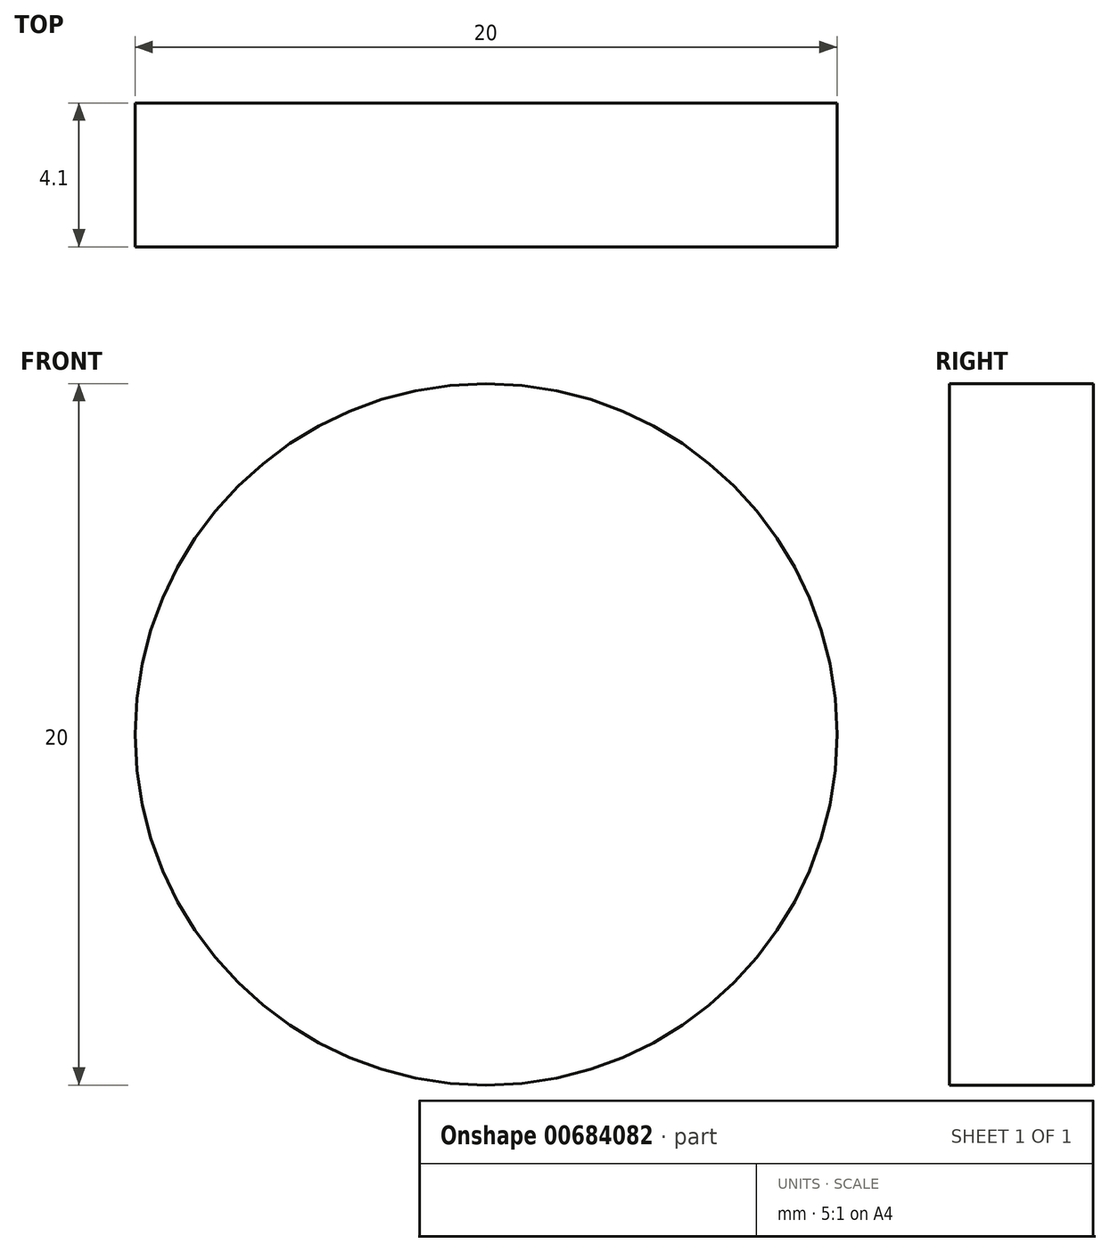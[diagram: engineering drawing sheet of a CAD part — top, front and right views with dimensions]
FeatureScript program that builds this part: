
annotation { "Feature Type Name" : "Feature", "Feature Type Description" : "" }
export const myFeature = defineFeature(function(context is Context, id is Id, definition is map)
    precondition{}
    {
        {
            var Q0;
            Q0=qCreatedBy(makeId("Front.planeOp"),FACE);
            var sketch = newSketch(context, id + "F0", { "sketchPlane" : qUnion([Q0])});
            skCircle(sketch, "E0", {"center": v(0, 0) * mm, "radius": 10 * mm});
            skSolve(sketch);
        }
        {
            var Q0;
            Q0=makeQuery(id+"F0.imprint","IMPRINT",FACE,{"disambiguationData":[TD([[makeQuery(id+"F0.imprint","IMPRINT",EDGE,{"derivedFrom":sQuery(id+"F0.wireOp",EDGE,"E0")}),1.0]])]});
            extrude(context, id + "F1", {"entities" : qUnion([Q0]), "depth" : 4.1 * mm, "offsetDistance" : 25 * mm});
        }
    });
